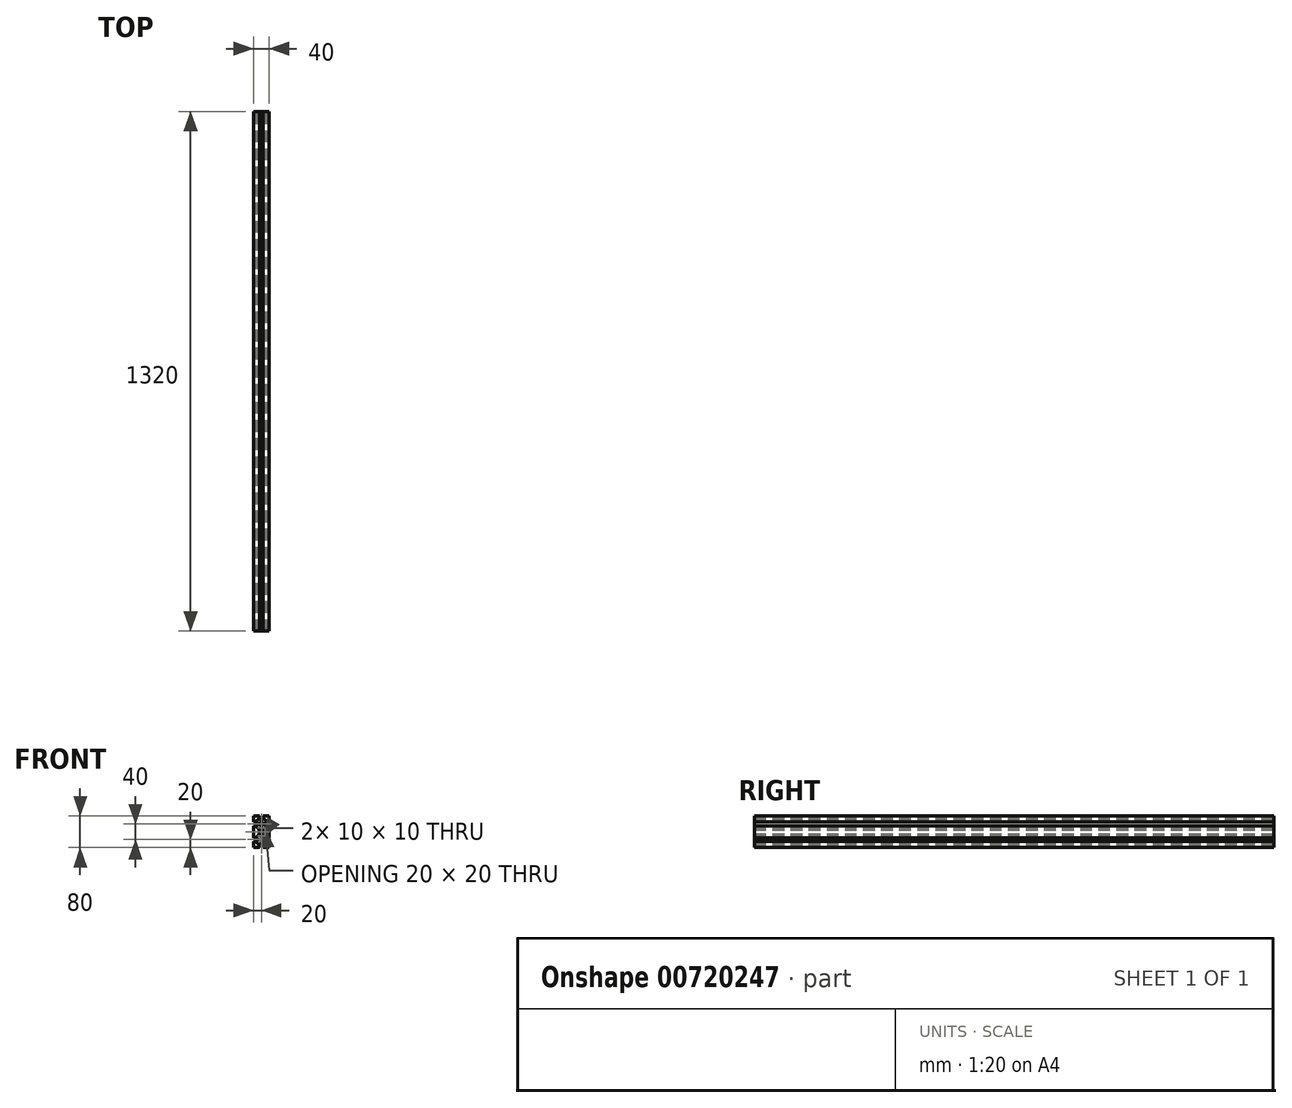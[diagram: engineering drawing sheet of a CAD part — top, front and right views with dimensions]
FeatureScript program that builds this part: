
annotation { "Feature Type Name" : "Feature", "Feature Type Description" : "" }
export const myFeature = defineFeature(function(context is Context, id is Id, definition is map)
    precondition{}
    {
        {
            var Q0;
            Q0=qCreatedBy(makeId("Front.planeOp"),FACE);
            var sketch = newSketch(context, id + "F0", { "sketchPlane" : qUnion([Q0])});
            skLineSegment(sketch, "E0.top", {"start": v(20, -20) * mm, "end": v(5, -20) * mm});
            skLineSegment(sketch, "E0.left", {"start": v(20, 20) * mm, "end": v(20, 5) * mm});
            skLineSegment(sketch, "E0.right", {"start": v(-20, 20) * mm, "end": v(-20, 5) * mm});
            skPoint(sketch, "E0.middle", {"position": v(0, 0) * mm});
            skLineSegment(sketch, "E1", {"start": v(0, 20) * mm, "end": v(0, -20) * mm, "construction": true});
            skLineSegment(sketch, "E2", {"start": v(-20, 0) * mm, "end": v(20, 0) * mm, "construction": true});
            skLineSegment(sketch, "E3", {"start": v(-20, 5) * mm, "end": v(-15, 5) * mm});
            skLineSegment(sketch, "E4", {"start": v(-20, -5) * mm, "end": v(-15, -5) * mm});
            skLineSegment(sketch, "E5", {"start": v(-5, 20) * mm, "end": v(-5, 15) * mm});
            skLineSegment(sketch, "E6", {"start": v(5, 20) * mm, "end": v(5, 15) * mm});
            skLineSegment(sketch, "E7", {"start": v(-10, 15) * mm, "end": v(-5, 15) * mm});
            skLineSegment(sketch, "E8", {"start": v(-10, -15) * mm, "end": v(-5, -15) * mm});
            skLineSegment(sketch, "E9", {"start": v(15, 10) * mm, "end": v(15, 5) * mm});
            skLineSegment(sketch, "E10", {"start": v(-15, 10) * mm, "end": v(-10, 5) * mm});
            skLineSegment(sketch, "E11", {"start": v(-10, 15) * mm, "end": v(-5, 10) * mm});
            skLineSegment(sketch, "E12", {"start": v(-15, -10) * mm, "end": v(-10, -5) * mm});
            skLineSegment(sketch, "E13", {"start": v(-10, -15) * mm, "end": v(-5, -10) * mm});
            skLineSegment(sketch, "E14.trimOffspring", {"start": v(20, -5) * mm, "end": v(20, -20) * mm});
            skLineSegment(sketch, "E15.trimOffspring", {"start": v(-20, -5) * mm, "end": v(-20, -20) * mm});
            skLineSegment(sketch, "E16.trimOffspring", {"start": v(-5, -20) * mm, "end": v(-20, -20) * mm});
            skLineSegment(sketch, "E17.trimOffspring", {"start": v(5, 15) * mm, "end": v(10, 15) * mm});
            skLineSegment(sketch, "E18.trimOffspring", {"start": v(-15, -5) * mm, "end": v(-15, -10) * mm});
            skLineSegment(sketch, "E19.trimOffspring", {"start": v(15, -5) * mm, "end": v(15, -10) * mm});
            skLineSegment(sketch, "E20.trimOffspring", {"start": v(5, -15) * mm, "end": v(10, -15) * mm});
            skLineSegment(sketch, "E21.trimOffspring", {"start": v(-5, 5) * mm, "end": v(-5, -5) * mm});
            skLineSegment(sketch, "E22.trimOffspring", {"start": v(5, 5) * mm, "end": v(5, -5) * mm});
            skLineSegment(sketch, "E23.trimOffspring", {"start": v(15, 5) * mm, "end": v(20, 5) * mm});
            skLineSegment(sketch, "E24.trimOffspring", {"start": v(15, -5) * mm, "end": v(20, -5) * mm});
            skLineSegment(sketch, "E25.trimOffspring", {"start": v(5, -15) * mm, "end": v(5, -20) * mm});
            skLineSegment(sketch, "E26.trimOffspring", {"start": v(-5, -15) * mm, "end": v(-5, -20) * mm});
            skLineSegment(sketch, "E27.trimOffspring", {"start": v(-5, -5) * mm, "end": v(5, -5) * mm});
            skLineSegment(sketch, "E28.trimOffspring", {"start": v(-5, 5) * mm, "end": v(5, 5) * mm});
            skLineSegment(sketch, "E29", {"start": v(10, 5) * mm, "end": v(10, -5) * mm});
            skLineSegment(sketch, "E30", {"start": v(-5, 10) * mm, "end": v(5, 10) * mm});
            skLineSegment(sketch, "E31", {"start": v(-10, 5) * mm, "end": v(-10, -5) * mm});
            skLineSegment(sketch, "E32", {"start": v(-5, -10) * mm, "end": v(5, -10) * mm});
            skLineSegment(sketch, "E33.trimOffspring", {"start": v(-15, 10) * mm, "end": v(-15, 5) * mm});
            skPoint(sketch, "E34.orphan", {"position": v(20, 15) * mm});
            skPoint(sketch, "E35.orphan", {"position": v(20, -15) * mm});
            skPoint(sketch, "E36.orphan", {"position": v(15, -20) * mm});
            skPoint(sketch, "E37.orphan", {"position": v(-15, -20) * mm});
            skLineSegment(sketch, "E38.trimOffspring", {"start": v(-5, 0) * mm, "end": v(0, -5) * mm});
            skLineSegment(sketch, "E39.trimOffspring", {"start": v(-5, 0) * mm, "end": v(0, 5) * mm});
            skLineSegment(sketch, "E40.trimOffspring", {"start": v(0, 5) * mm, "end": v(5, 0) * mm});
            skLineSegment(sketch, "E41.trimOffspring", {"start": v(5, 10) * mm, "end": v(10, 15) * mm});
            skLineSegment(sketch, "E42.trimOffspring", {"start": v(10, 5) * mm, "end": v(15, 10) * mm});
            skLineSegment(sketch, "E43.trimOffspring", {"start": v(10, -5) * mm, "end": v(15, -10) * mm});
            skLineSegment(sketch, "E44.trimOffspring", {"start": v(5, -10) * mm, "end": v(10, -15) * mm});
            skLineSegment(sketch, "E45.trimOffspring", {"start": v(0, -5) * mm, "end": v(5, 0) * mm});
            skLineSegment(sketch, "E46.bottom", {"start": v(20, 60) * mm, "end": v(5, 60) * mm});
            skLineSegment(sketch, "E46.left", {"start": v(20, 60) * mm, "end": v(20, 45) * mm});
            skLineSegment(sketch, "E46.right", {"start": v(-20, 60) * mm, "end": v(-20, 45) * mm});
            skPoint(sketch, "E46.middle", {"position": v(0, 40) * mm});
            skLineSegment(sketch, "E47", {"start": v(0, 60) * mm, "end": v(0, 20) * mm, "construction": true});
            skLineSegment(sketch, "E48", {"start": v(-20, 40) * mm, "end": v(20, 40) * mm, "construction": true});
            skLineSegment(sketch, "E49", {"start": v(-20, 45) * mm, "end": v(-15, 45) * mm});
            skLineSegment(sketch, "E50", {"start": v(-20, 35) * mm, "end": v(-15, 35) * mm});
            skLineSegment(sketch, "E51", {"start": v(-5, 60) * mm, "end": v(-5, 55) * mm});
            skLineSegment(sketch, "E52", {"start": v(5, 60) * mm, "end": v(5, 55) * mm});
            skLineSegment(sketch, "E53", {"start": v(-10, 55) * mm, "end": v(-5, 55) * mm});
            skLineSegment(sketch, "E54", {"start": v(-10, 25) * mm, "end": v(-5, 25) * mm});
            skLineSegment(sketch, "E55", {"start": v(15, 50) * mm, "end": v(15, 45) * mm});
            skLineSegment(sketch, "E56", {"start": v(-15, 50) * mm, "end": v(-10, 45) * mm});
            skLineSegment(sketch, "E57", {"start": v(-10, 55) * mm, "end": v(-5, 50) * mm});
            skLineSegment(sketch, "E58", {"start": v(-15, 30) * mm, "end": v(-10, 35) * mm});
            skLineSegment(sketch, "E59", {"start": v(-10, 25) * mm, "end": v(-5, 30) * mm});
            skLineSegment(sketch, "E60.trimOffspring", {"start": v(20, 35) * mm, "end": v(20, 20) * mm});
            skLineSegment(sketch, "E61.trimOffspring", {"start": v(-20, 35) * mm, "end": v(-20, 20) * mm});
            skLineSegment(sketch, "E62.trimOffspring", {"start": v(-5, 60) * mm, "end": v(-20, 60) * mm});
            skLineSegment(sketch, "E63.trimOffspring", {"start": v(5, 55) * mm, "end": v(10, 55) * mm});
            skLineSegment(sketch, "E64.trimOffspring", {"start": v(-15, 35) * mm, "end": v(-15, 30) * mm});
            skLineSegment(sketch, "E65.trimOffspring", {"start": v(15, 35) * mm, "end": v(15, 30) * mm});
            skLineSegment(sketch, "E66.trimOffspring", {"start": v(5, 25) * mm, "end": v(10, 25) * mm});
            skLineSegment(sketch, "E67.trimOffspring", {"start": v(-5, 45) * mm, "end": v(-5, 35) * mm});
            skLineSegment(sketch, "E68.trimOffspring", {"start": v(5, 45) * mm, "end": v(5, 35) * mm});
            skLineSegment(sketch, "E69.trimOffspring", {"start": v(15, 45) * mm, "end": v(20, 45) * mm});
            skLineSegment(sketch, "E70.trimOffspring", {"start": v(15, 35) * mm, "end": v(20, 35) * mm});
            skLineSegment(sketch, "E71.trimOffspring", {"start": v(5, 25) * mm, "end": v(5, 20) * mm});
            skLineSegment(sketch, "E72.trimOffspring", {"start": v(-5, 25) * mm, "end": v(-5, 20) * mm});
            skLineSegment(sketch, "E73.trimOffspring", {"start": v(-5, 35) * mm, "end": v(5, 35) * mm});
            skLineSegment(sketch, "E74.trimOffspring", {"start": v(-5, 45) * mm, "end": v(5, 45) * mm});
            skLineSegment(sketch, "E75", {"start": v(10, 45) * mm, "end": v(10, 35) * mm});
            skLineSegment(sketch, "E76", {"start": v(-5, 50) * mm, "end": v(5, 50) * mm});
            skLineSegment(sketch, "E77", {"start": v(-10, 45) * mm, "end": v(-10, 35) * mm});
            skLineSegment(sketch, "E78", {"start": v(-5, 30) * mm, "end": v(5, 30) * mm});
            skLineSegment(sketch, "E79.trimOffspring", {"start": v(-15, 50) * mm, "end": v(-15, 45) * mm});
            skPoint(sketch, "E80.orphan", {"position": v(20, 55) * mm});
            skPoint(sketch, "E81.orphan", {"position": v(20, 25) * mm});
            skPoint(sketch, "E82.orphan", {"position": v(15, 20) * mm});
            skLineSegment(sketch, "E83.trimOffspring", {"start": v(-5, 40) * mm, "end": v(0, 35) * mm});
            skLineSegment(sketch, "E84.trimOffspring", {"start": v(-5, 40) * mm, "end": v(0, 45) * mm});
            skLineSegment(sketch, "E85.trimOffspring", {"start": v(0, 45) * mm, "end": v(5, 40) * mm});
            skLineSegment(sketch, "E86.trimOffspring", {"start": v(5, 50) * mm, "end": v(10, 55) * mm});
            skLineSegment(sketch, "E87.trimOffspring", {"start": v(10, 45) * mm, "end": v(15, 50) * mm});
            skLineSegment(sketch, "E88.trimOffspring", {"start": v(10, 35) * mm, "end": v(15, 30) * mm});
            skLineSegment(sketch, "E89.trimOffspring", {"start": v(5, 30) * mm, "end": v(10, 25) * mm});
            skLineSegment(sketch, "E90.trimOffspring", {"start": v(0, 35) * mm, "end": v(5, 40) * mm});
            skSolve(sketch);
        }
        {
            var Q0;
            Q0=makeQuery(id+"F0.imprint","IMPRINT",FACE,{"disambiguationData":[TD([[makeQuery(id+"F0.imprint","IMPRINT",EDGE,{"derivedFrom":sQuery(id+"F0.wireOp",EDGE,"E0.top")}),-1.0]])]});
            extrude(context, id + "F1", {"entities" : qUnion([Q0]), "depth" : 1320 * mm, "offsetDistance" : 25 * mm});
        }
    });
